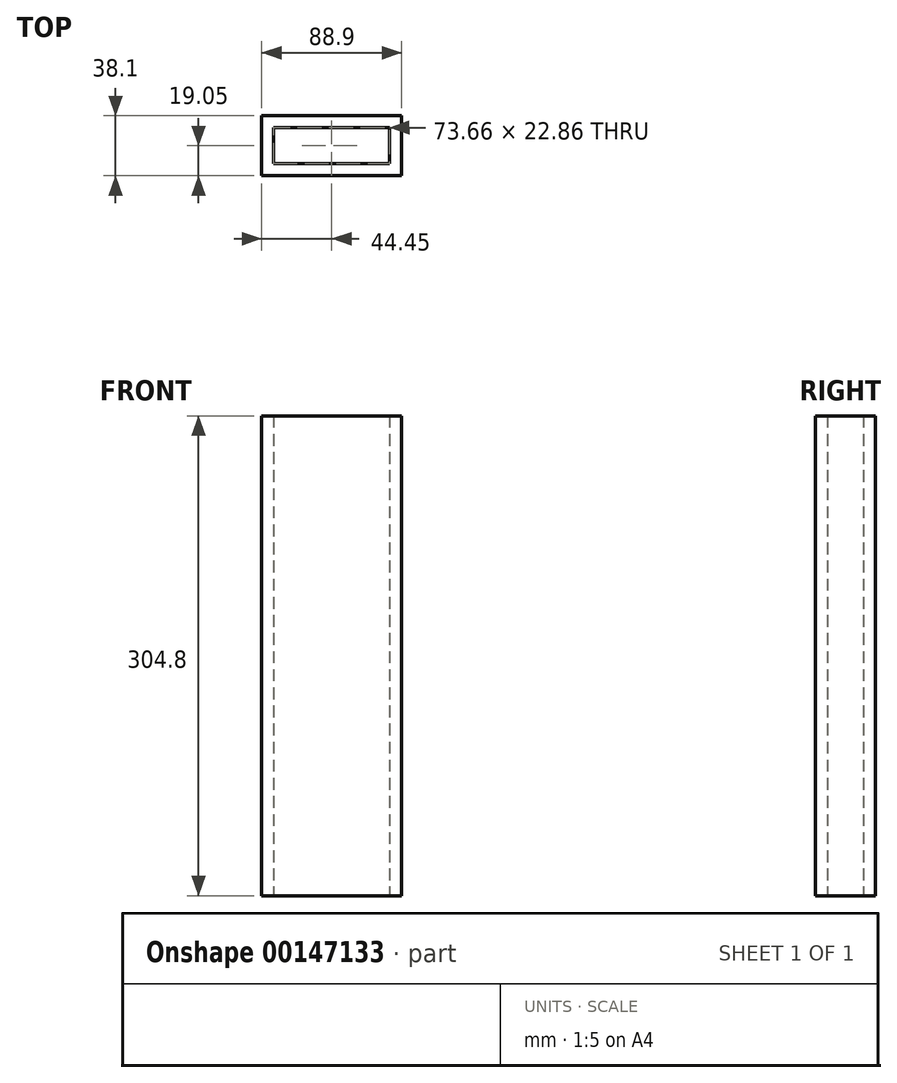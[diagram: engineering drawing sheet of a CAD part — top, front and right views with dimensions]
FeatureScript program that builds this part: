
annotation { "Feature Type Name" : "Feature", "Feature Type Description" : "" }
export const myFeature = defineFeature(function(context is Context, id is Id, definition is map)
    precondition{}
    {
        {
            var Q0;
            Q0=qCreatedBy(makeId("Top.planeOp"),FACE);
            var sketch = newSketch(context, id + "F0", { "sketchPlane" : qUnion([Q0])});
            skLineSegment(sketch, "E0", {"start": v(-44.45, 0) * mm, "end": v(-44.45, 19.05) * mm});
            skLineSegment(sketch, "E1", {"start": v(-44.45, 19.05) * mm, "end": v(44.45, 19.05) * mm});
            skLineSegment(sketch, "E2", {"start": v(44.45, 19.05) * mm, "end": v(44.45, 0) * mm});
            skLineSegment(sketch, "E3", {"start": v(44.45, 0) * mm, "end": v(36.83, 0) * mm});
            skLineSegment(sketch, "E4", {"start": v(36.83, 0) * mm, "end": v(36.83, 11.43) * mm});
            skLineSegment(sketch, "E5", {"start": v(36.83, 11.43) * mm, "end": v(-36.83, 11.43) * mm});
            skLineSegment(sketch, "E6", {"start": v(-36.83, 11.43) * mm, "end": v(-36.83, 0) * mm});
            skLineSegment(sketch, "E7", {"start": v(-36.83, 0) * mm, "end": v(-44.45, 0) * mm});
            skSolve(sketch);
        }
        {
            var Q0;
            Q0=makeQuery(id+"F0.imprint","IMPRINT",FACE,{"disambiguationData":[TD([[makeQuery(id+"F0.imprint","IMPRINT",EDGE,{"derivedFrom":sQuery(id+"F0.wireOp",EDGE,"E0")}),-1.0]])]});
            extrude(context, id + "F1", {"entities" : qUnion([Q0]), "depth" : 304.8 * mm});
        }
        {
            var Q0;
            Q0=makeQuery(id+"F1.opExtrude","SWEPT_BODY",BODY,{"disambiguationData":[OSD([sQuery(id+"F0.wireOp",EDGE,"E0"),sQuery(id+"F0.wireOp",EDGE,"E1"),sQuery(id+"F0.wireOp",EDGE,"E2"),sQuery(id+"F0.wireOp",EDGE,"E3"),sQuery(id+"F0.wireOp",EDGE,"E4"),sQuery(id+"F0.wireOp",EDGE,"E5"),sQuery(id+"F0.wireOp",EDGE,"E6"),sQuery(id+"F0.wireOp",EDGE,"E7")])]});
            var Q1;
            Q1=qCreatedBy(makeId("Front.planeOp"),FACE);
            mirror(context, id + "F2", {"operationType" : NewBodyOperationType.ADD, "entities" : qUnion([Q0]), "mirrorPlane" : qUnion([Q1])});
        }
    });
